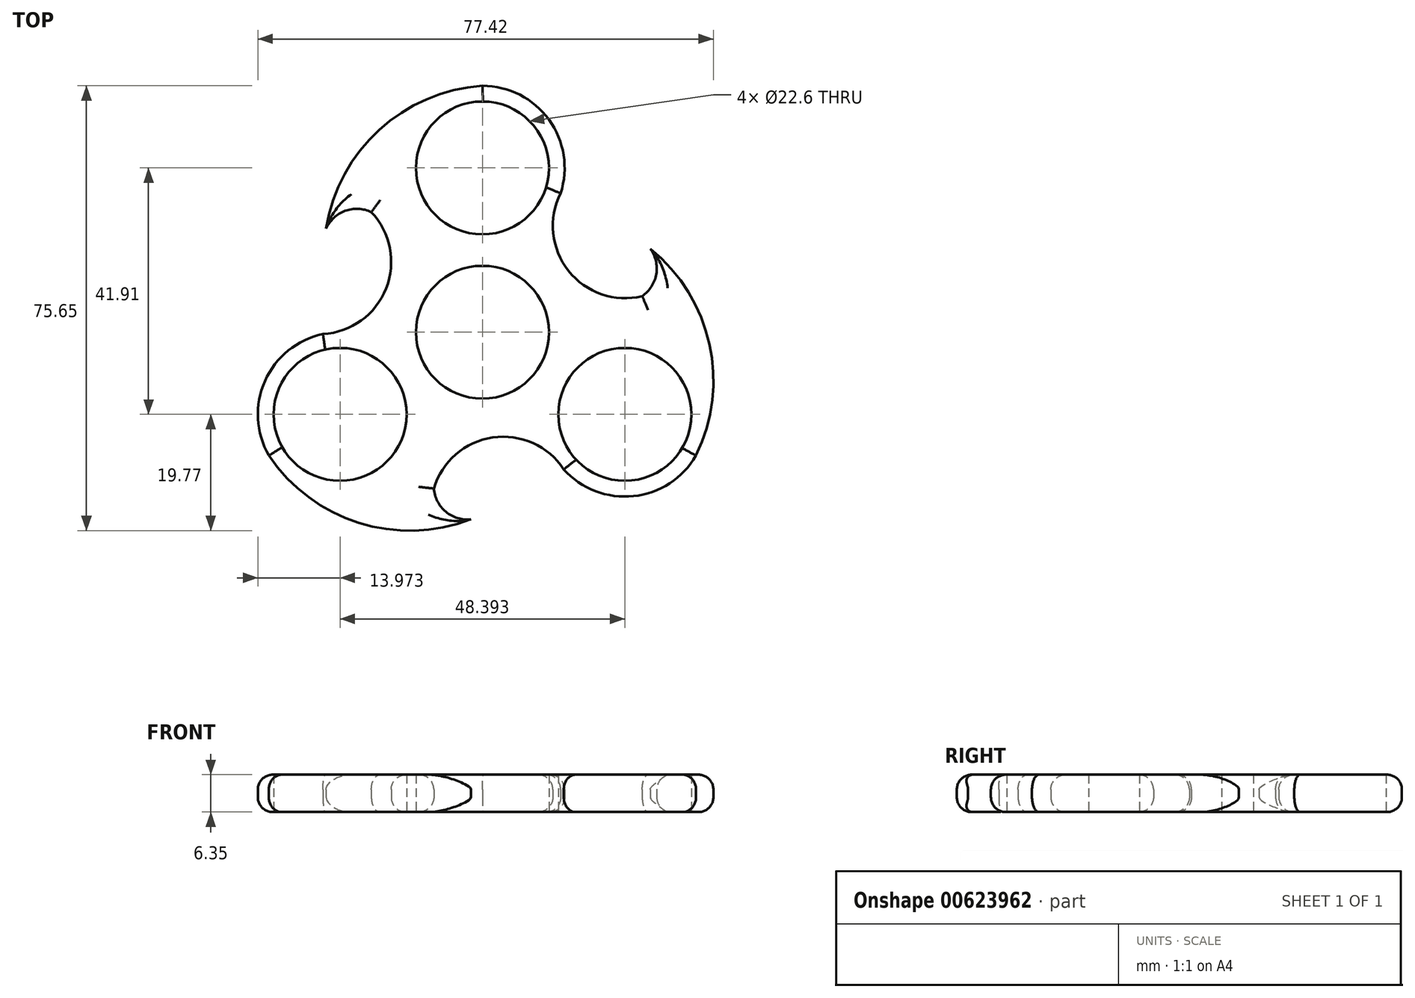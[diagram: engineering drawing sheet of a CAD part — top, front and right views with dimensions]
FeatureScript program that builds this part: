
annotation { "Feature Type Name" : "Feature", "Feature Type Description" : "" }
export const myFeature = defineFeature(function(context is Context, id is Id, definition is map)
    precondition{}
    {
        {
            var Q0;
            Q0=qCreatedBy(makeId("Top.planeOp"),FACE);
            var sketch = newSketch(context, id + "F0", { "sketchPlane" : qUnion([Q0])});
            skCircle(sketch, "E0", {"center": v(0, 0) * mm, "radius": 11.3 * mm});
            skCircle(sketch, "E1", {"center": v(0, 27.94) * mm, "radius": 11.3 * mm});
            skCircle(sketch, "E2.1.0", {"center": v(-24.2, -13.97) * mm, "radius": 11.3 * mm});
            skCircle(sketch, "E2.2.0", {"center": v(24.2, -13.97) * mm, "radius": 11.3 * mm});
            skArc(sketch, "E3", {"start": v(12.54, 21.78) * mm, "mid": v(10.8, 36.8) * mm, "end": v(-3.59, 41.44) * mm});
            skArc(sketch, "E4", {"start": v(-25.13, -0.03) * mm, "mid": v(-37.27, -9.05) * mm, "end": v(-34.1, -23.83) * mm});
            skArc(sketch, "E5", {"start": v(12.6, -21.75) * mm, "mid": v(26.47, -27.75) * mm, "end": v(37.68, -17.61) * mm});
            skPoint(sketch, "E6.start.orphan", {"position": v(0, 41.91) * mm});
            skArc(sketch, "E7", {"start": v(-18.88, 20.44) * mm, "mid": v(-23.33, 20.64) * mm, "end": v(-26.57, 17.6) * mm});
            skPoint(sketch, "E8.startSnap0", {"position": v(-15.2, 14.45) * mm});
            skArc(sketch, "E9", {"start": v(0, 41.91) * mm, "mid": v(-17.55, 34.4) * mm, "end": v(-26.57, 17.6) * mm});
            skArc(sketch, "E10.1.0", {"start": v(-36.3, -20.95) * mm, "mid": v(-21.03, -32.4) * mm, "end": v(-1.95, -31.81) * mm});
            skArc(sketch, "E10.1.1", {"start": v(-8.26, -26.57) * mm, "mid": v(-6.21, -30.52) * mm, "end": v(-1.95, -31.81) * mm});
            skArc(sketch, "E10.2.0", {"start": v(36.3, -20.96) * mm, "mid": v(38.57, -2) * mm, "end": v(28.53, 14.22) * mm});
            skArc(sketch, "E10.2.1", {"start": v(27.14, 6.14) * mm, "mid": v(29.54, 9.88) * mm, "end": v(28.53, 14.22) * mm});
            skArc(sketch, "E11", {"start": v(13.81, -23.32) * mm, "mid": v(1.74, -17.9) * mm, "end": v(-8.26, -26.57) * mm});
            skArc(sketch, "E12.1.0", {"start": v(13.29, 23.62) * mm, "mid": v(14.63, 10.46) * mm, "end": v(27.14, 6.14) * mm});
            skArc(sketch, "E12.2.0", {"start": v(-27.1, -0.3) * mm, "mid": v(-16.37, 7.44) * mm, "end": v(-18.88, 20.44) * mm});
            skPoint(sketch, "E13.end.orphan", {"position": v(-15.2, 4.25) * mm});
            skSolve(sketch);
        }
        {
            var Q0;
            Q0=makeQuery(id+"F0.imprint","IMPRINT",FACE,{"disambiguationData":[TD([[makeQuery(id+"F0.imprint","IMPRINT",EDGE,{"derivedFrom":sQuery(id+"F0.wireOp",EDGE,"E1")}),-1.0]])]});
            var Q1;
            Q1=makeQuery(id+"F0.imprint","IMPRINT",FACE,{"disambiguationData":[TD([[makeQuery(id+"F0.imprint","IMPRINT",EDGE,{"derivedFrom":sQuery(id+"F0.wireOp",EDGE,"E2.2.0")}),-1.0]])]});
            var Q2;
            Q2=makeQuery(id+"F0.imprint","IMPRINT",FACE,{"disambiguationData":[TD([[makeQuery(id+"F0.imprint","IMPRINT",EDGE,{"derivedFrom":sQuery(id+"F0.wireOp",EDGE,"E2.1.0")}),-1.0]])]});
            var Q3;
            Q3=makeQuery(id+"F0.imprint","IMPRINT",FACE,{"disambiguationData":[TD([[makeQuery(id+"F0.imprint","IMPRINT",EDGE,{"derivedFrom":sQuery(id+"F0.wireOp",EDGE,"4O9khdKf-2qk6-6eEU-YUye-EU3OGTiNBHui")}),-1.0]])]});
            var Q4;
            Q4=makeQuery(id+"F0.imprint","IMPRINT",FACE,{"disambiguationData":[TD([[makeQuery(id+"F0.imprint","IMPRINT",EDGE,{"derivedFrom":sQuery(id+"F0.wireOp",EDGE,"E0")}),-1.0]])]});
            extrude(context, id + "F1", {"entities" : qUnion([Q0, Q1, Q2, Q3, Q4]), "depth" : 6.35 * mm, "offsetDistance" : 25 * mm});
        }
        {
            var Q0;
            Q0=makeQuery(id+"F1.opExtrude","CAP_FACE",FACE,{"disambiguationData":[OSD([sQuery(id+"F0.wireOp",EDGE,"E0"),sQuery(id+"F0.wireOp",EDGE,"E1"),sQuery(id+"F0.wireOp",EDGE,"E2.1.0"),sQuery(id+"F0.wireOp",EDGE,"E2.2.0"),sQuery(id+"F0.wireOp",EDGE,"E3"),sQuery(id+"F0.wireOp",EDGE,"E4"),sQuery(id+"F0.wireOp",EDGE,"E5"),sQuery(id+"F0.wireOp",EDGE,"UQbOZFWg-WlBi-0oOe-1g90-T6ZUHGj5ubKu"),sQuery(id+"F0.wireOp",EDGE,"9Wr71UDA-qCNy-LS3O-krRt-GMsWMRKGUIlI"),sQuery(id+"F0.wireOp",EDGE,"dLQuffVX-C3dp-mtUo-6BRO-KFHYK7wXLIDl")])],"isStart":false});
            var sketch = newSketch(context, id + "F2", { "sketchPlane" : qUnion([Q0])});
            skSolve(sketch);
        }
        {
            var Q0;
            Q0=makeQuery(id+"F1.opExtrude","CAP_EDGE",EDGE,{"disambiguationData":[OSD([sQuery(id+"F0.wireOp",EDGE,"E10.1.0")])],"isStart":false});
            var Q1;
            Q1=makeQuery(id+"F1.opExtrude","CAP_EDGE",EDGE,{"disambiguationData":[OSD([sQuery(id+"F0.wireOp",EDGE,"E8")])],"isStart":false});
            var Q2;
            Q2=makeQuery(id+"F1.opExtrude","CAP_EDGE",EDGE,{"disambiguationData":[OSD([sQuery(id+"F0.wireOp",EDGE,"E13")])],"isStart":false});
            var Q3;
            Q3=makeQuery(id+"F1.opExtrude","CAP_EDGE",EDGE,{"disambiguationData":[OSD([sQuery(id+"F0.wireOp",EDGE,"E9")])],"isStart":false});
            var Q4;
            Q4=makeQuery(id+"F1.opExtrude","CAP_EDGE",EDGE,{"disambiguationData":[OSD([sQuery(id+"F0.wireOp",EDGE,"E3")])],"isStart":false});
            var Q5;
            Q5=makeQuery(id+"F1.opExtrude","CAP_EDGE",EDGE,{"disambiguationData":[OSD([sQuery(id+"F0.wireOp",EDGE,"E10.2.3")])],"isStart":false});
            var Q6;
            Q6=makeQuery(id+"F1.opExtrude","CAP_EDGE",EDGE,{"disambiguationData":[OSD([sQuery(id+"F0.wireOp",EDGE,"E10.2.2")])],"isStart":false});
            var Q7;
            Q7=makeQuery(id+"F1.opExtrude","CAP_EDGE",EDGE,{"disambiguationData":[OSD([sQuery(id+"F0.wireOp",EDGE,"E10.2.1")])],"isStart":false});
            var Q8;
            Q8=makeQuery(id+"F1.opExtrude","CAP_EDGE",EDGE,{"disambiguationData":[OSD([sQuery(id+"F0.wireOp",EDGE,"E10.1.2")])],"isStart":false});
            var Q9;
            Q9=makeQuery(id+"F1.opExtrude","CAP_EDGE",EDGE,{"disambiguationData":[OSD([sQuery(id+"F0.wireOp",EDGE,"E10.1.1")])],"isStart":false});
            var Q10;
            Q10=makeQuery(id+"F1.opExtrude","CAP_EDGE",EDGE,{"disambiguationData":[OSD([sQuery(id+"F0.wireOp",EDGE,"E10.2.0")])],"isStart":false});
            var Q11;
            Q11=makeQuery(id+"F1.opExtrude","CAP_EDGE",EDGE,{"disambiguationData":[OSD([sQuery(id+"F0.wireOp",EDGE,"E10.1.3")])],"isStart":false});
            var Q12;
            Q12=makeQuery(id+"F1.opExtrude","CAP_EDGE",EDGE,{"disambiguationData":[OSD([sQuery(id+"F0.wireOp",EDGE,"E7")])],"isStart":false});
            var Q13;
            Q13=makeQuery(id+"F1.opExtrude","CAP_EDGE",EDGE,{"disambiguationData":[OSD([sQuery(id+"F0.wireOp",EDGE,"E10.2.0")])],"isStart":true});
            var Q14;
            Q14=makeQuery(id+"F1.opExtrude","CAP_EDGE",EDGE,{"disambiguationData":[OSD([sQuery(id+"F0.wireOp",EDGE,"E10.2.2")])],"isStart":true});
            var Q15;
            Q15=makeQuery(id+"F1.opExtrude","CAP_EDGE",EDGE,{"disambiguationData":[OSD([sQuery(id+"F0.wireOp",EDGE,"E10.2.3")])],"isStart":true});
            var Q16;
            Q16=makeQuery(id+"F1.opExtrude","CAP_EDGE",EDGE,{"disambiguationData":[OSD([sQuery(id+"F0.wireOp",EDGE,"E9")])],"isStart":true});
            var Q17;
            Q17=makeQuery(id+"F1.opExtrude","CAP_EDGE",EDGE,{"disambiguationData":[OSD([sQuery(id+"F0.wireOp",EDGE,"E8")])],"isStart":true});
            var Q18;
            Q18=makeQuery(id+"F1.opExtrude","CAP_EDGE",EDGE,{"disambiguationData":[OSD([sQuery(id+"F0.wireOp",EDGE,"E13")])],"isStart":true});
            var Q19;
            Q19=makeQuery(id+"F1.opExtrude","CAP_EDGE",EDGE,{"disambiguationData":[OSD([sQuery(id+"F0.wireOp",EDGE,"E10.1.0")])],"isStart":true});
            var Q20;
            Q20=makeQuery(id+"F1.opExtrude","CAP_EDGE",EDGE,{"disambiguationData":[OSD([sQuery(id+"F0.wireOp",EDGE,"E10.1.1")])],"isStart":true});
            var Q21;
            Q21=makeQuery(id+"F1.opExtrude","CAP_EDGE",EDGE,{"disambiguationData":[OSD([sQuery(id+"F0.wireOp",EDGE,"E10.1.2")])],"isStart":true});
            var Q22;
            Q22=makeQuery(id+"F1.opExtrude","CAP_EDGE",EDGE,{"disambiguationData":[OSD([sQuery(id+"F0.wireOp",EDGE,"E10.1.3")])],"isStart":true});
            var Q23;
            Q23=makeQuery(id+"F1.opExtrude","CAP_EDGE",EDGE,{"disambiguationData":[OSD([sQuery(id+"F0.wireOp",EDGE,"E11")])],"isStart":true});
            var Q24;
            Q24=makeQuery(id+"F1.opExtrude","CAP_EDGE",EDGE,{"disambiguationData":[OSD([sQuery(id+"F0.wireOp",EDGE,"E5")])],"isStart":true});
            var Q25;
            Q25=makeQuery(id+"F1.opExtrude","CAP_EDGE",EDGE,{"disambiguationData":[OSD([sQuery(id+"F0.wireOp",EDGE,"E5")])],"isStart":false});
            var Q26;
            Q26=makeQuery(id+"F1.opExtrude","CAP_EDGE",EDGE,{"disambiguationData":[OSD([sQuery(id+"F0.wireOp",EDGE,"E11")])],"isStart":false});
            var Q27;
            Q27=makeQuery(id+"F1.opExtrude","CAP_EDGE",EDGE,{"disambiguationData":[OSD([sQuery(id+"F0.wireOp",EDGE,"E12.2.0")])],"isStart":false});
            var Q28;
            Q28=makeQuery(id+"F1.opExtrude","CAP_EDGE",EDGE,{"disambiguationData":[OSD([sQuery(id+"F0.wireOp",EDGE,"E4")])],"isStart":false});
            var Q29;
            Q29=makeQuery(id+"F1.opExtrude","CAP_EDGE",EDGE,{"disambiguationData":[OSD([sQuery(id+"F0.wireOp",EDGE,"E12.1.0")])],"isStart":false});
            var Q30;
            Q30=makeQuery(id+"F1.opExtrude","CAP_EDGE",EDGE,{"disambiguationData":[OSD([sQuery(id+"F0.wireOp",EDGE,"E12.2.0")])],"isStart":true});
            var Q31;
            Q31=makeQuery(id+"F1.opExtrude","CAP_EDGE",EDGE,{"disambiguationData":[OSD([sQuery(id+"F0.wireOp",EDGE,"E7")])],"isStart":true});
            var Q32;
            Q32=makeQuery(id+"F1.opExtrude","CAP_EDGE",EDGE,{"disambiguationData":[OSD([sQuery(id+"F0.wireOp",EDGE,"E4")])],"isStart":true});
            var Q33;
            Q33=makeQuery(id+"F1.opExtrude","CAP_EDGE",EDGE,{"disambiguationData":[OSD([sQuery(id+"F0.wireOp",EDGE,"E3")])],"isStart":true});
            var Q34;
            Q34=makeQuery(id+"F1.opExtrude","CAP_EDGE",EDGE,{"disambiguationData":[OSD([sQuery(id+"F0.wireOp",EDGE,"E12.1.0")])],"isStart":true});
            var Q35;
            Q35=makeQuery(id+"F1.opExtrude","CAP_EDGE",EDGE,{"disambiguationData":[OSD([sQuery(id+"F0.wireOp",EDGE,"E10.2.1")])],"isStart":true});
            fillet(context, id + "F3", {"entities" : qUnion([Q0, Q1, Q2, Q3, Q4, Q5, Q6, Q7, Q8, Q9, Q10, Q11, Q12, Q13, Q14, Q15, Q16, Q17, Q18, Q19, Q20, Q21, Q22, Q23, Q24, Q25, Q26, Q27, Q28, Q29, Q30, Q31, Q32, Q33, Q34, Q35]), "radius" : 2.54 * mm, "tangentPropagation" : true, "allowEdgeOverflow" : false});
        }
        {
            var Q0;
            Q0=makeQuery(id+"F1.opExtrude","CAP_FACE",FACE,{"disambiguationData":[OSD([sQuery(id+"F0.wireOp",EDGE,"E0"),sQuery(id+"F0.wireOp",EDGE,"E1"),sQuery(id+"F0.wireOp",EDGE,"E2.1.0"),sQuery(id+"F0.wireOp",EDGE,"E2.2.0"),sQuery(id+"F0.wireOp",EDGE,"E3"),sQuery(id+"F0.wireOp",EDGE,"E4"),sQuery(id+"F0.wireOp",EDGE,"E5"),sQuery(id+"F0.wireOp",EDGE,"E7"),sQuery(id+"F0.wireOp",EDGE,"E9"),sQuery(id+"F0.wireOp",EDGE,"E10.1.0"),sQuery(id+"F0.wireOp",EDGE,"E10.1.1"),sQuery(id+"F0.wireOp",EDGE,"E10.2.0"),sQuery(id+"F0.wireOp",EDGE,"E10.2.1"),sQuery(id+"F0.wireOp",EDGE,"E11"),sQuery(id+"F0.wireOp",EDGE,"E12.1.0"),sQuery(id+"F0.wireOp",EDGE,"E12.2.0")])],"isStart":true});
            var sketch = newSketch(context, id + "F4", { "sketchPlane" : qUnion([Q0])});
            skPoint(sketch, "E14", {"position": v(11.3, 0) * mm});
            skSolve(sketch);
        }
        {
            var Q0;
            Q0=makeQuery(id+"F4.imprint","IMPRINT",FACE,{"disambiguationData":[TD([[makeQuery(id+"F4.imprint","IMPRINT",EDGE,{"derivedFrom":makeQuery(id+"F1.opExtrude","CAP_EDGE",EDGE,{"disambiguationData":[OSD([sQuery(id+"F0.wireOp",EDGE,"E2.1.0")])],"isStart":true})}),-1.0]])]});
            var Q1;
            Q1=makeQuery(id+"F4.imprint","IMPRINT",FACE,{"disambiguationData":[TD([[makeQuery(id+"F4.imprint","IMPRINT",EDGE,{"derivedFrom":makeQuery(id+"F1.opExtrude","CAP_EDGE",EDGE,{"disambiguationData":[OSD([sQuery(id+"F0.wireOp",EDGE,"E0")])],"isStart":true})}),-1.0]])]});
            var Q2;
            Q2=makeQuery(id+"F4.imprint","IMPRINT",FACE,{"disambiguationData":[TD([[makeQuery(id+"F4.imprint","IMPRINT",EDGE,{"derivedFrom":makeQuery(id+"F1.opExtrude","CAP_EDGE",EDGE,{"disambiguationData":[OSD([sQuery(id+"F0.wireOp",EDGE,"E2.2.0")])],"isStart":true})}),-1.0]])]});
            var Q3;
            Q3=makeQuery(id+"F4.imprint","IMPRINT",FACE,{"disambiguationData":[TD([[makeQuery(id+"F4.imprint","IMPRINT",EDGE,{"derivedFrom":makeQuery(id+"F1.opExtrude","CAP_EDGE",EDGE,{"disambiguationData":[OSD([sQuery(id+"F0.wireOp",EDGE,"E1")])],"isStart":true})}),-1.0]])]});
            extrude(context, id + "F5", {"entities" : qUnion([Q0, Q1, Q2, Q3]), "operationType" : NewBodyOperationType.REMOVE, "endBound" : BoundingType.THROUGH_ALL, "oppositeDirection" : true, "depth" : 25 * mm, "offsetDistance" : 25 * mm});
        }
    });
